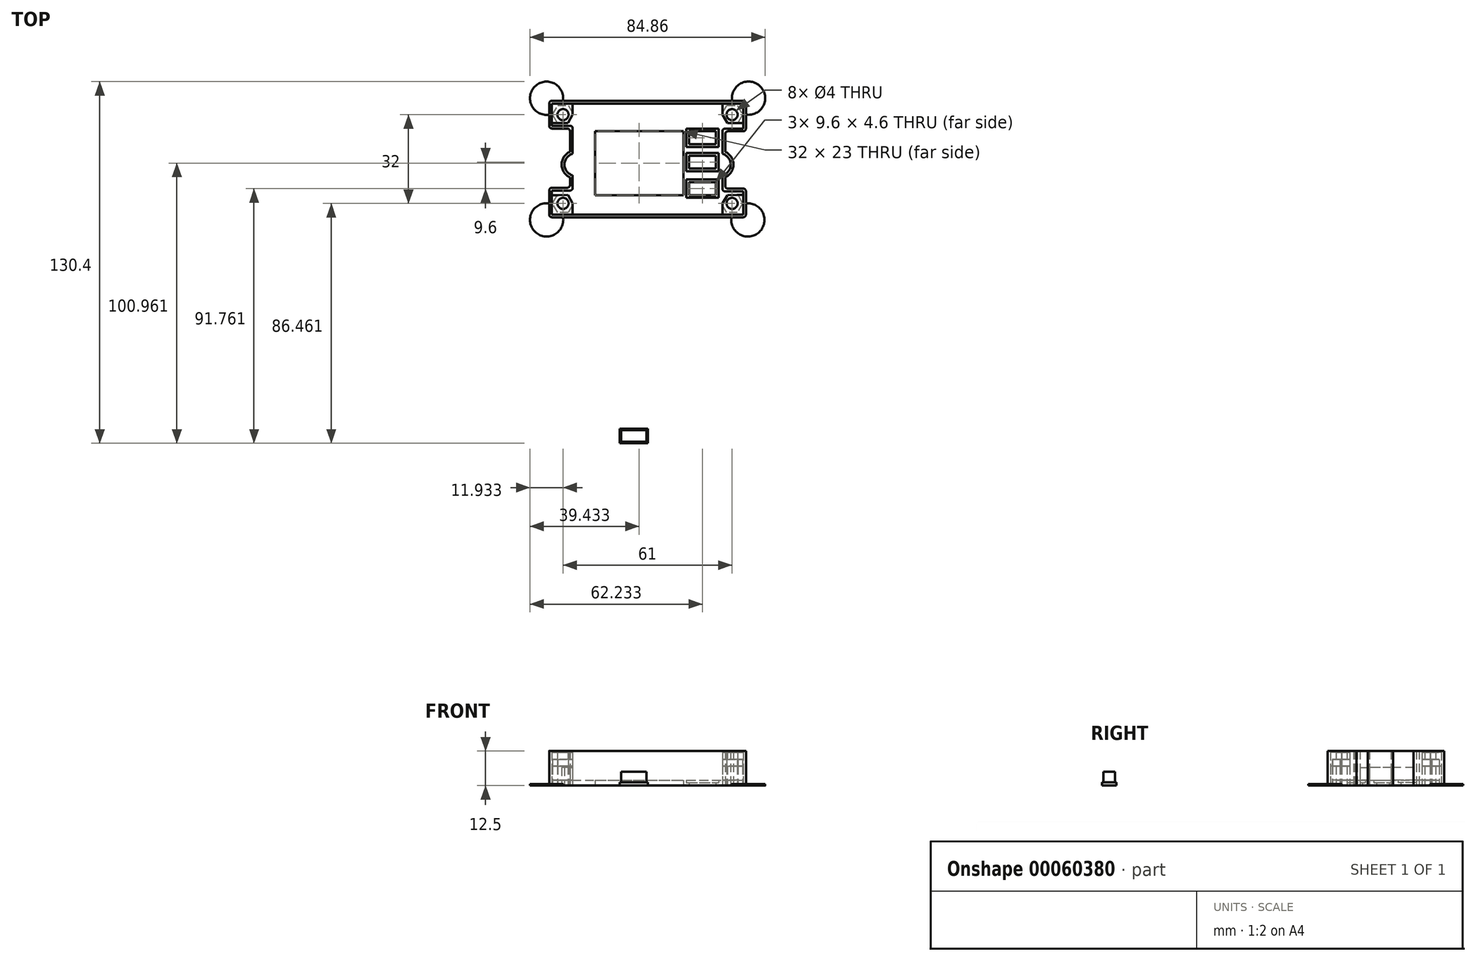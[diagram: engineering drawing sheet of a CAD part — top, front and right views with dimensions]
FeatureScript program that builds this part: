
annotation { "Feature Type Name" : "Feature", "Feature Type Description" : "" }
export const myFeature = defineFeature(function(context is Context, id is Id, definition is map)
    precondition{}
    {
        {
            var Q0;
            Q0=qCreatedBy(makeId("Top.planeOp"),FACE);
            var sketch = newSketch(context, id + "F0", { "sketchPlane" : qUnion([Q0])});
            skCircle(sketch, "E0.cCircle", {"center": v(0, 0) * mm, "radius": 3 * mm, "construction": true});
            skLineSegment(sketch, "E0.0", {"start": v(1.73, 3) * mm, "end": v(3.46, 0) * mm});
            skLineSegment(sketch, "E0.1", {"start": v(3.46, 0) * mm, "end": v(1.74, -3) * mm});
            skLineSegment(sketch, "E0.2", {"start": v(1.74, -3) * mm, "end": v(-1.73, -3) * mm});
            skLineSegment(sketch, "E0.3", {"start": v(-1.73, -3) * mm, "end": v(-3.46, 0) * mm});
            skLineSegment(sketch, "E0.4", {"start": v(-3.46, 0) * mm, "end": v(-1.74, 3) * mm});
            skLineSegment(sketch, "E0.5", {"start": v(-1.74, 3) * mm, "end": v(1.73, 3) * mm});
            skPoint(sketch, "E0.0.midPoint", {"position": v(2.6, 1.5) * mm});
            skCircle(sketch, "E1", {"center": v(0, 0) * mm, "radius": 1.5 * mm});
            skLineSegment(sketch, "E2.bottom", {"start": v(-12.76, 69.41) * mm, "end": v(56.24, 69.41) * mm});
            skLineSegment(sketch, "E2.top", {"start": v(-12.76, 29.41) * mm, "end": v(56.24, 29.41) * mm});
            skLineSegment(sketch, "E2.left", {"start": v(-12.76, 69.41) * mm, "end": v(-12.76, 29.41) * mm});
            skLineSegment(sketch, "E2.right", {"start": v(56.24, 69.41) * mm, "end": v(56.24, 29.41) * mm});
            skPoint(sketch, "E3.0.midPoint", {"position": v(-6.16, 66.92) * mm});
            skLineSegment(sketch, "E3.3", {"start": v(-10.48, 62.4) * mm, "end": v(-12.22, 65.4) * mm, "construction": true});
            skLineSegment(sketch, "E3.2", {"start": v(-7.02, 62.41) * mm, "end": v(-10.48, 62.4) * mm});
            skLineSegment(sketch, "E3.1", {"start": v(-5.3, 65.42) * mm, "end": v(-7.02, 62.41) * mm});
            skLineSegment(sketch, "E3.0", {"start": v(-7.03, 68.41) * mm, "end": v(-5.3, 65.42) * mm, "construction": true});
            skLineSegment(sketch, "E3.4", {"start": v(-12.22, 65.4) * mm, "end": v(-10.5, 68.4) * mm, "construction": true});
            skLineSegment(sketch, "E3.5", {"start": v(-10.5, 68.4) * mm, "end": v(-7.03, 68.41) * mm, "construction": true});
            skCircle(sketch, "E4", {"center": v(-8.76, 65.41) * mm, "radius": 1.5 * mm, "construction": true});
            skCircle(sketch, "E3.cCircle", {"center": v(-8.76, 65.41) * mm, "radius": 3 * mm, "construction": true});
            skPoint(sketch, "E5.0.midPoint", {"position": v(-6.16, 34.92) * mm});
            skLineSegment(sketch, "E5.3", {"start": v(-10.48, 30.4) * mm, "end": v(-12.22, 33.4) * mm, "construction": true});
            skLineSegment(sketch, "E5.2", {"start": v(-7.02, 30.41) * mm, "end": v(-10.48, 30.4) * mm, "construction": true});
            skLineSegment(sketch, "E5.1", {"start": v(-5.3, 33.42) * mm, "end": v(-7.02, 30.41) * mm, "construction": true});
            skLineSegment(sketch, "E5.0", {"start": v(-7.03, 36.41) * mm, "end": v(-5.3, 33.42) * mm});
            skLineSegment(sketch, "E5.4", {"start": v(-12.22, 33.4) * mm, "end": v(-10.5, 36.4) * mm, "construction": true});
            skLineSegment(sketch, "E5.5", {"start": v(-10.5, 36.4) * mm, "end": v(-7.03, 36.41) * mm});
            skCircle(sketch, "E6", {"center": v(-8.76, 33.41) * mm, "radius": 1.5 * mm, "construction": true});
            skCircle(sketch, "E5.cCircle", {"center": v(-8.76, 33.41) * mm, "radius": 3 * mm, "construction": true});
            skPoint(sketch, "E7.0.midPoint", {"position": v(54.84, 66.92) * mm});
            skLineSegment(sketch, "E7.3", {"start": v(50.52, 62.4) * mm, "end": v(48.78, 65.4) * mm});
            skLineSegment(sketch, "E7.2", {"start": v(53.98, 62.41) * mm, "end": v(50.52, 62.4) * mm});
            skLineSegment(sketch, "E7.1", {"start": v(55.7, 65.42) * mm, "end": v(53.98, 62.41) * mm, "construction": true});
            skLineSegment(sketch, "E7.0", {"start": v(53.97, 68.41) * mm, "end": v(55.7, 65.42) * mm, "construction": true});
            skLineSegment(sketch, "E7.4", {"start": v(48.78, 65.4) * mm, "end": v(50.5, 68.4) * mm, "construction": true});
            skLineSegment(sketch, "E7.5", {"start": v(50.5, 68.4) * mm, "end": v(53.97, 68.41) * mm, "construction": true});
            skCircle(sketch, "E8", {"center": v(52.24, 65.41) * mm, "radius": 1.5 * mm, "construction": true});
            skCircle(sketch, "E7.cCircle", {"center": v(52.24, 65.41) * mm, "radius": 3 * mm, "construction": true});
            skPoint(sketch, "E9.0.midPoint", {"position": v(54.84, 34.92) * mm});
            skLineSegment(sketch, "E9.3", {"start": v(50.52, 30.4) * mm, "end": v(48.78, 33.4) * mm, "construction": true});
            skLineSegment(sketch, "E9.2", {"start": v(53.98, 30.41) * mm, "end": v(50.52, 30.4) * mm, "construction": true});
            skLineSegment(sketch, "E9.1", {"start": v(55.7, 33.42) * mm, "end": v(53.98, 30.41) * mm, "construction": true});
            skLineSegment(sketch, "E9.0", {"start": v(53.97, 36.41) * mm, "end": v(55.7, 33.42) * mm, "construction": true});
            skLineSegment(sketch, "E9.4", {"start": v(48.78, 33.4) * mm, "end": v(50.5, 36.4) * mm});
            skLineSegment(sketch, "E9.5", {"start": v(50.5, 36.4) * mm, "end": v(53.97, 36.41) * mm});
            skCircle(sketch, "E10", {"center": v(52.24, 33.41) * mm, "radius": 1.5 * mm, "construction": true});
            skCircle(sketch, "E9.cCircle", {"center": v(52.24, 33.41) * mm, "radius": 3 * mm, "construction": true});
            skLineSegment(sketch, "E11", {"start": v(48.78, 33.4) * mm, "end": v(48.78, 29.41) * mm});
            skLineSegment(sketch, "E12", {"start": v(53.97, 36.41) * mm, "end": v(56.24, 36.41) * mm});
            skCircle(sketch, "E13.0", {"center": v(52.24, 33.41) * mm, "radius": 2 * mm});
            skLineSegment(sketch, "E14.0", {"start": v(50.34, 30.1) * mm, "end": v(48.52, 33.25) * mm});
            skLineSegment(sketch, "E14.1", {"start": v(54.15, 30.11) * mm, "end": v(50.34, 30.1) * mm});
            skLineSegment(sketch, "E14.2", {"start": v(56.05, 33.42) * mm, "end": v(54.15, 30.11) * mm});
            skLineSegment(sketch, "E14.3", {"start": v(54.23, 36.56) * mm, "end": v(56.05, 33.42) * mm});
            skLineSegment(sketch, "E15", {"start": v(-5.3, 33.42) * mm, "end": v(-5.3, 29.41) * mm});
            skLineSegment(sketch, "E16", {"start": v(-10.5, 36.4) * mm, "end": v(-12.76, 36.4) * mm});
            skLineSegment(sketch, "E17", {"start": v(-10.48, 62.4) * mm, "end": v(-12.76, 62.4) * mm});
            skLineSegment(sketch, "E18", {"start": v(-5.3, 65.42) * mm, "end": v(-5.3, 69.41) * mm});
            skLineSegment(sketch, "E19", {"start": v(53.98, 62.41) * mm, "end": v(56.24, 62.42) * mm});
            skLineSegment(sketch, "E20", {"start": v(48.78, 65.4) * mm, "end": v(48.78, 69.41) * mm});
            skCircle(sketch, "E21.0", {"center": v(52.24, 65.41) * mm, "radius": 2 * mm});
            skCircle(sketch, "E22.0", {"center": v(-8.76, 65.41) * mm, "radius": 2 * mm});
            skCircle(sketch, "E23.0", {"center": v(-8.76, 33.41) * mm, "radius": 2 * mm});
            skLineSegment(sketch, "E24.0", {"start": v(-6.86, 68.71) * mm, "end": v(-5.03, 65.57) * mm});
            skLineSegment(sketch, "E24.1", {"start": v(-10.67, 68.7) * mm, "end": v(-6.86, 68.71) * mm});
            skLineSegment(sketch, "E24.2", {"start": v(-12.57, 65.4) * mm, "end": v(-10.67, 68.7) * mm});
            skLineSegment(sketch, "E24.3", {"start": v(-10.74, 62.26) * mm, "end": v(-12.57, 65.4) * mm});
            skLineSegment(sketch, "E25.0", {"start": v(-12.57, 33.4) * mm, "end": v(-10.76, 36.56) * mm});
            skLineSegment(sketch, "E25.1", {"start": v(-10.66, 30.1) * mm, "end": v(-12.57, 33.4) * mm});
            skLineSegment(sketch, "E25.2", {"start": v(-6.85, 30.11) * mm, "end": v(-10.66, 30.1) * mm});
            skLineSegment(sketch, "E25.3", {"start": v(-5.03, 33.27) * mm, "end": v(-6.85, 30.11) * mm});
            skLineSegment(sketch, "E26.0", {"start": v(56.05, 65.42) * mm, "end": v(49.92, 54.75) * mm});
            skLineSegment(sketch, "E26.1", {"start": v(54.14, 68.71) * mm, "end": v(56.05, 65.42) * mm});
            skLineSegment(sketch, "E26.2", {"start": v(50.33, 68.7) * mm, "end": v(54.14, 68.71) * mm});
            skLineSegment(sketch, "E26.3", {"start": v(48.52, 65.55) * mm, "end": v(50.33, 68.7) * mm});
            skPoint(sketch, "E27", {"position": v(2.74, 36.41) * mm});
            skLineSegment(sketch, "E28.bottom", {"start": v(2.74, 36.41) * mm, "end": v(34.74, 36.41) * mm});
            skLineSegment(sketch, "E28.top", {"start": v(2.74, 59.41) * mm, "end": v(34.74, 59.41) * mm});
            skLineSegment(sketch, "E28.left", {"start": v(2.74, 36.41) * mm, "end": v(2.74, 59.41) * mm});
            skLineSegment(sketch, "E28.right", {"start": v(34.74, 36.41) * mm, "end": v(34.74, 59.41) * mm});
            skPoint(sketch, "E29", {"position": v(36.74, 59.41) * mm});
            skLineSegment(sketch, "E30.bottom", {"start": v(36.74, 59.41) * mm, "end": v(46.34, 59.41) * mm});
            skLineSegment(sketch, "E30.top", {"start": v(36.74, 54.81) * mm, "end": v(46.34, 54.81) * mm});
            skLineSegment(sketch, "E30.left", {"start": v(36.74, 59.41) * mm, "end": v(36.74, 54.81) * mm});
            skLineSegment(sketch, "E30.right", {"start": v(46.34, 59.41) * mm, "end": v(46.34, 54.81) * mm});
            skLineSegment(sketch, "E31.bottom", {"start": v(36.74, 36.41) * mm, "end": v(46.34, 36.41) * mm});
            skLineSegment(sketch, "E31.top", {"start": v(36.74, 41.01) * mm, "end": v(46.34, 41.01) * mm});
            skLineSegment(sketch, "E31.left", {"start": v(36.74, 36.41) * mm, "end": v(36.74, 41.01) * mm});
            skLineSegment(sketch, "E31.right", {"start": v(46.34, 36.41) * mm, "end": v(46.34, 41.01) * mm});
            skLineSegment(sketch, "E32.bottom", {"start": v(36.74, 46.01) * mm, "end": v(46.34, 46.01) * mm});
            skLineSegment(sketch, "E32.top", {"start": v(36.74, 50.61) * mm, "end": v(46.34, 50.61) * mm});
            skLineSegment(sketch, "E32.left", {"start": v(36.74, 46.01) * mm, "end": v(36.74, 50.61) * mm});
            skLineSegment(sketch, "E32.right", {"start": v(46.34, 46.01) * mm, "end": v(46.34, 50.61) * mm});
            skLineSegment(sketch, "E33.0", {"start": v(-13.76, 38.03) * mm, "end": v(-13.76, 29.41) * mm});
            skLineSegment(sketch, "E33.1", {"start": v(-12.76, 70.41) * mm, "end": v(56.24, 70.41) * mm});
            skLineSegment(sketch, "E33.2", {"start": v(57.24, 69.41) * mm, "end": v(57.24, 60.41) * mm});
            skLineSegment(sketch, "E33.3", {"start": v(-12.76, 28.41) * mm, "end": v(56.24, 28.41) * mm});
            skPoint(sketch, "E34", {"position": v(-13.76, 61.41) * mm});
            skPoint(sketch, "E35", {"position": v(-13.76, 40.41) * mm});
            skLineSegment(sketch, "E36", {"start": v(-13.76, 61.41) * mm, "end": v(-12.76, 61.41) * mm});
            skLineSegment(sketch, "E37", {"start": v(-13.76, 40.41) * mm, "end": v(-12.76, 40.41) * mm});
            skLineSegment(sketch, "E38.bottom", {"start": v(13.09, -34.33) * mm, "end": v(22.29, -34.33) * mm});
            skLineSegment(sketch, "E38.top", {"start": v(13.09, -38.53) * mm, "end": v(22.29, -38.53) * mm});
            skLineSegment(sketch, "E38.left", {"start": v(13.09, -34.33) * mm, "end": v(13.09, -38.53) * mm});
            skLineSegment(sketch, "E38.right", {"start": v(22.29, -34.33) * mm, "end": v(22.29, -38.53) * mm});
            skLineSegment(sketch, "E39.0", {"start": v(12.09, -33.33) * mm, "end": v(23.29, -33.33) * mm});
            skLineSegment(sketch, "E39.1", {"start": v(12.09, -33.33) * mm, "end": v(12.09, -39.53) * mm});
            skLineSegment(sketch, "E39.2", {"start": v(12.09, -39.53) * mm, "end": v(23.29, -39.53) * mm});
            skLineSegment(sketch, "E39.3", {"start": v(23.29, -33.33) * mm, "end": v(23.29, -39.53) * mm});
            skLineSegment(sketch, "E40.bottom", {"start": v(12.2, -48.35) * mm, "end": v(21.4, -48.35) * mm});
            skLineSegment(sketch, "E40.top", {"start": v(12.2, -52.55) * mm, "end": v(21.4, -52.55) * mm});
            skLineSegment(sketch, "E40.left", {"start": v(12.2, -48.35) * mm, "end": v(12.2, -52.55) * mm});
            skLineSegment(sketch, "E40.right", {"start": v(21.4, -48.35) * mm, "end": v(21.4, -52.55) * mm});
            skLineSegment(sketch, "E41.0", {"start": v(11.7, -47.85) * mm, "end": v(21.9, -47.85) * mm});
            skLineSegment(sketch, "E41.1", {"start": v(11.7, -47.85) * mm, "end": v(11.7, -53.05) * mm});
            skLineSegment(sketch, "E41.2", {"start": v(11.7, -53.05) * mm, "end": v(21.9, -53.05) * mm});
            skLineSegment(sketch, "E41.3", {"start": v(21.9, -47.85) * mm, "end": v(21.9, -53.05) * mm});
            skArc(sketch, "E42", {"start": v(57.24, 65.42) * mm, "mid": v(62.4, 75.6) * mm, "end": v(52.24, 70.41) * mm});
            skArc(sketch, "E43", {"start": v(52.24, 29.41) * mm, "mid": v(61.67, 22.77) * mm, "end": v(57.24, 33.42) * mm});
            skArc(sketch, "E44", {"start": v(-13.76, 33.4) * mm, "mid": v(-18.92, 23.23) * mm, "end": v(-8.76, 28.41) * mm});
            skArc(sketch, "E45", {"start": v(-8.76, 70.41) * mm, "mid": v(-18.93, 75.57) * mm, "end": v(-13.76, 65.4) * mm});
            skLineSegment(sketch, "E46.0", {"start": v(35.74, 53.81) * mm, "end": v(47.34, 53.81) * mm});
            skLineSegment(sketch, "E46.1", {"start": v(35.74, 60.41) * mm, "end": v(35.74, 53.81) * mm});
            skLineSegment(sketch, "E46.2", {"start": v(35.74, 60.41) * mm, "end": v(47.34, 60.41) * mm});
            skLineSegment(sketch, "E46.3", {"start": v(47.34, 60.41) * mm, "end": v(47.34, 53.81) * mm});
            skLineSegment(sketch, "E47.0", {"start": v(35.74, 51.61) * mm, "end": v(47.34, 51.61) * mm});
            skLineSegment(sketch, "E47.1", {"start": v(35.74, 45.01) * mm, "end": v(35.74, 51.61) * mm});
            skLineSegment(sketch, "E47.2", {"start": v(35.74, 45.01) * mm, "end": v(47.34, 45.01) * mm});
            skLineSegment(sketch, "E47.3", {"start": v(47.34, 45.01) * mm, "end": v(47.34, 51.61) * mm});
            skLineSegment(sketch, "E48.0", {"start": v(35.74, 42.01) * mm, "end": v(47.34, 42.01) * mm});
            skLineSegment(sketch, "E48.1", {"start": v(35.74, 35.41) * mm, "end": v(35.74, 42.01) * mm});
            skLineSegment(sketch, "E48.2", {"start": v(35.74, 35.41) * mm, "end": v(47.34, 35.41) * mm});
            skLineSegment(sketch, "E48.3", {"start": v(47.34, 35.41) * mm, "end": v(47.34, 42.01) * mm});
            skLineSegment(sketch, "E49", {"start": v(-4.26, 32.41) * mm, "end": v(47.74, 32.41) * mm, "construction": true});
            skLineSegment(sketch, "E50", {"start": v(47.74, 32.41) * mm, "end": v(47.74, 68.41) * mm, "construction": true});
            skLineSegment(sketch, "E51", {"start": v(47.74, 68.41) * mm, "end": v(-4.26, 68.41) * mm, "construction": true});
            skLineSegment(sketch, "E52", {"start": v(-4.26, 68.41) * mm, "end": v(-4.26, 32.41) * mm, "construction": true});
            skArc(sketch, "E53", {"start": v(-4.26, 50.41) * mm, "mid": v(-7.26, 47.41) * mm, "end": v(-4.26, 44.41) * mm, "construction": true});
            skArc(sketch, "E54", {"start": v(47.74, 44.41) * mm, "mid": v(50.74, 47.41) * mm, "end": v(47.74, 50.41) * mm, "construction": true});
            skArc(sketch, "E55.0", {"start": v(-4.26, 51.41) * mm, "mid": v(-4.76, 51.38) * mm, "end": v(-5.26, 51.28) * mm});
            skArc(sketch, "E56.0", {"start": v(47.74, 43.41) * mm, "mid": v(48.33, 43.45) * mm, "end": v(48.9, 43.58) * mm});
            skLineSegment(sketch, "E57", {"start": v(-12.76, 61.41) * mm, "end": v(-6.26, 61.41) * mm});
            skLineSegment(sketch, "E58", {"start": v(-5.26, 60.41) * mm, "end": v(-5.26, 51.28) * mm});
            skLineSegment(sketch, "E59", {"start": v(-12.76, 38.03) * mm, "end": v(-6.26, 38.03) * mm});
            skLineSegment(sketch, "E60", {"start": v(-5.26, 39.03) * mm, "end": v(-5.26, 43.54) * mm});
            skArc(sketch, "E61", {"start": v(-5.26, 51.28) * mm, "mid": v(-8.26, 47.41) * mm, "end": v(-5.26, 43.54) * mm});
            skArc(sketch, "E62", {"start": v(-5.26, 43.54) * mm, "mid": v(-4.76, 43.44) * mm, "end": v(-4.26, 43.41) * mm});
            skLineSegment(sketch, "E63.0", {"start": v(-12.76, 39.03) * mm, "end": v(-7.26, 39.03) * mm});
            skLineSegment(sketch, "E63.1", {"start": v(-12.76, 60.41) * mm, "end": v(-7.26, 60.41) * mm});
            skLineSegment(sketch, "E63.2", {"start": v(-6.26, 59.41) * mm, "end": v(-6.26, 52) * mm});
            skArc(sketch, "E63.3", {"start": v(-6.26, 52) * mm, "mid": v(-9.26, 47.41) * mm, "end": v(-6.26, 42.83) * mm});
            skLineSegment(sketch, "E63.4", {"start": v(-6.26, 40.03) * mm, "end": v(-6.26, 42.83) * mm});
            skLineSegment(sketch, "E64", {"start": v(-12.76, 60.41) * mm, "end": v(-12.76, 60.41) * mm});
            skLineSegment(sketch, "E65", {"start": v(-12.76, 39.03) * mm, "end": v(-12.76, 39.03) * mm});
            skArc(sketch, "E66.filletArc", {"start": v(-12.76, 39.03) * mm, "mid": v(-13.46, 38.74) * mm, "end": v(-13.76, 38.03) * mm});
            skLineSegment(sketch, "E67", {"start": v(-13.76, 69.41) * mm, "end": v(-13.76, 61.41) * mm});
            skPoint(sketch, "E68.visualSharp", {"position": v(-13.76, 60.41) * mm});
            skArc(sketch, "E68.filletArc", {"start": v(-13.76, 61.41) * mm, "mid": v(-13.46, 60.7) * mm, "end": v(-12.76, 60.41) * mm});
            skPoint(sketch, "E69.visualSharp", {"position": v(-5.26, 61.41) * mm});
            skArc(sketch, "E69.filletArc", {"start": v(-5.26, 60.41) * mm, "mid": v(-5.55, 61.12) * mm, "end": v(-6.26, 61.41) * mm});
            skArc(sketch, "E70.filletArc", {"start": v(-6.26, 59.41) * mm, "mid": v(-6.55, 60.12) * mm, "end": v(-7.26, 60.41) * mm});
            skPoint(sketch, "E71.visualSharp", {"position": v(-6.26, 39.03) * mm});
            skArc(sketch, "E71.filletArc", {"start": v(-7.26, 39.03) * mm, "mid": v(-6.55, 39.32) * mm, "end": v(-6.26, 40.03) * mm});
            skPoint(sketch, "E72.visualSharp", {"position": v(-5.26, 38.03) * mm});
            skArc(sketch, "E72.filletArc", {"start": v(-6.26, 38.03) * mm, "mid": v(-5.55, 38.32) * mm, "end": v(-5.26, 39.03) * mm});
            skLineSegment(sketch, "E73", {"start": v(-6.26, 59.41) * mm, "end": v(-5.26, 59.41) * mm});
            skLineSegment(sketch, "E74", {"start": v(-6.26, 40.03) * mm, "end": v(-5.26, 40.03) * mm});
            skLineSegment(sketch, "E75", {"start": v(56.24, 60.41) * mm, "end": v(49.74, 60.41) * mm});
            skLineSegment(sketch, "E76", {"start": v(48.74, 59.41) * mm, "end": v(48.74, 51.28) * mm});
            skLineSegment(sketch, "E77", {"start": v(48.74, 43.54) * mm, "end": v(48.74, 38.74) * mm});
            skLineSegment(sketch, "E78", {"start": v(49.74, 37.74) * mm, "end": v(56.24, 37.74) * mm});
            skArc(sketch, "E79", {"start": v(48.74, 51.28) * mm, "mid": v(48.25, 51.38) * mm, "end": v(47.74, 51.41) * mm});
            skArc(sketch, "E80", {"start": v(48.9, 43.58) * mm, "mid": v(51.74, 47.5) * mm, "end": v(48.74, 51.28) * mm});
            skLineSegment(sketch, "E81.0", {"start": v(56.24, 59.41) * mm, "end": v(50.74, 59.41) * mm});
            skLineSegment(sketch, "E81.1", {"start": v(49.74, 58.41) * mm, "end": v(49.74, 52) * mm});
            skLineSegment(sketch, "E82.0", {"start": v(50.74, 38.74) * mm, "end": v(56.24, 38.74) * mm});
            skLineSegment(sketch, "E83", {"start": v(49.74, 42.83) * mm, "end": v(49.74, 39.74) * mm});
            skArc(sketch, "E84", {"start": v(49.74, 42.83) * mm, "mid": v(52.74, 47.41) * mm, "end": v(49.74, 52) * mm});
            skPoint(sketch, "E85.visualSharp", {"position": v(49.74, 59.41) * mm});
            skArc(sketch, "E85.filletArc", {"start": v(50.74, 59.41) * mm, "mid": v(50.04, 59.12) * mm, "end": v(49.74, 58.41) * mm});
            skPoint(sketch, "E86.visualSharp", {"position": v(49.74, 38.74) * mm});
            skArc(sketch, "E86.filletArc", {"start": v(49.74, 39.74) * mm, "mid": v(50.04, 39.04) * mm, "end": v(50.74, 38.74) * mm});
            skLineSegment(sketch, "E87", {"start": v(56.24, 38.74) * mm, "end": v(56.24, 38.74) * mm});
            skLineSegment(sketch, "E88", {"start": v(56.24, 59.41) * mm, "end": v(56.24, 59.41) * mm});
            skArc(sketch, "E89.filletArc", {"start": v(56.24, 59.41) * mm, "mid": v(56.95, 59.7) * mm, "end": v(57.24, 60.41) * mm});
            skLineSegment(sketch, "E90", {"start": v(57.24, 29.41) * mm, "end": v(57.24, 37.74) * mm});
            skPoint(sketch, "E91.visualSharp", {"position": v(57.24, 38.74) * mm});
            skArc(sketch, "E91.filletArc", {"start": v(57.24, 37.74) * mm, "mid": v(56.95, 38.45) * mm, "end": v(56.24, 38.74) * mm});
            skPoint(sketch, "E92.visualSharp", {"position": v(48.74, 37.74) * mm});
            skArc(sketch, "E92.filletArc", {"start": v(48.74, 38.74) * mm, "mid": v(49.04, 38.04) * mm, "end": v(49.74, 37.74) * mm});
            skPoint(sketch, "E93.visualSharp", {"position": v(48.74, 60.41) * mm});
            skArc(sketch, "E93.filletArc", {"start": v(49.74, 60.41) * mm, "mid": v(49.04, 60.12) * mm, "end": v(48.74, 59.41) * mm});
            skPoint(sketch, "E94.visualSharp", {"position": v(57.24, 28.41) * mm});
            skArc(sketch, "E94.filletArc", {"start": v(56.24, 28.41) * mm, "mid": v(56.95, 28.7) * mm, "end": v(57.24, 29.41) * mm});
            skPoint(sketch, "E95.visualSharp", {"position": v(-13.76, 28.41) * mm});
            skArc(sketch, "E95.filletArc", {"start": v(-13.76, 29.41) * mm, "mid": v(-13.46, 28.7) * mm, "end": v(-12.76, 28.41) * mm});
            skPoint(sketch, "E96.visualSharp", {"position": v(57.24, 70.41) * mm});
            skArc(sketch, "E96.filletArc", {"start": v(57.24, 69.41) * mm, "mid": v(56.95, 70.12) * mm, "end": v(56.24, 70.41) * mm});
            skPoint(sketch, "E97.visualSharp", {"position": v(-13.76, 70.41) * mm});
            skArc(sketch, "E97.filletArc", {"start": v(-12.76, 70.41) * mm, "mid": v(-13.46, 70.12) * mm, "end": v(-13.76, 69.41) * mm});
            skSolve(sketch);
        }
        {
            var Q0;
            {var subQ12=sQuery(id+"F0.wireOp",EDGE,"E14.1");Q0=makeQuery(id+"F0.imprint","IMPRINT",FACE,{"disambiguationData":[TD([[makeQuery(id+"F0.imprint","IMPRINT",EDGE,{"derivedFrom":subQ12}),1.0]])]});}
            var Q1;
            {var subQ6=sQuery(id+"F0.wireOp",EDGE,"E9.4");Q1=makeQuery(id+"F0.imprint","IMPRINT",FACE,{"disambiguationData":[TD([[makeQuery(id+"F0.imprint","IMPRINT",EDGE,{"derivedFrom":subQ6}),-1.0]])]});}
            var Q2;
            {var subQ5=sQuery(id+"F0.wireOp",EDGE,"E25.1");Q2=makeQuery(id+"F0.imprint","IMPRINT",FACE,{"disambiguationData":[TD([[makeQuery(id+"F0.imprint","IMPRINT",EDGE,{"derivedFrom":subQ5}),1.0]])]});}
            var Q3;
            {var subQ5=sQuery(id+"F0.wireOp",EDGE,"E5.0");Q3=makeQuery(id+"F0.imprint","IMPRINT",FACE,{"disambiguationData":[TD([[makeQuery(id+"F0.imprint","IMPRINT",EDGE,{"derivedFrom":subQ5}),-1.0]])]});}
            var Q4;
            {var subQ11=sQuery(id+"F0.wireOp",EDGE,"E24.1");Q4=makeQuery(id+"F0.imprint","IMPRINT",FACE,{"disambiguationData":[TD([[makeQuery(id+"F0.imprint","IMPRINT",EDGE,{"derivedFrom":subQ11}),1.0]])]});}
            var Q5;
            {var subQ5=sQuery(id+"F0.wireOp",EDGE,"E3.2");Q5=makeQuery(id+"F0.imprint","IMPRINT",FACE,{"disambiguationData":[TD([[makeQuery(id+"F0.imprint","IMPRINT",EDGE,{"derivedFrom":subQ5}),-1.0]])]});}
            var Q6;
            {var subQ7=sQuery(id+"F0.wireOp",EDGE,"E26.1");Q6=makeQuery(id+"F0.imprint","IMPRINT",FACE,{"disambiguationData":[TD([[makeQuery(id+"F0.imprint","IMPRINT",EDGE,{"derivedFrom":subQ7}),1.0]])]});}
            var Q7;
            {var subQ1=sQuery(id+"F0.wireOp",EDGE,"E7.3");Q7=makeQuery(id+"F0.imprint","IMPRINT",FACE,{"disambiguationData":[TD([[makeQuery(id+"F0.imprint","IMPRINT",EDGE,{"derivedFrom":subQ1}),-1.0]])]});}
            extrude(context, id + "F1", {"entities" : qUnion([Q0, Q1, Q2, Q3, Q4, Q5, Q6, Q7]), "depth" : 7 * mm});
        }
        {
            var Q0;
            {var subQ12=sQuery(id+"F0.wireOp",EDGE,"E14.1");Q0=makeQuery(id+"F0.imprint","IMPRINT",FACE,{"disambiguationData":[TD([[makeQuery(id+"F0.imprint","IMPRINT",EDGE,{"derivedFrom":subQ12}),1.0]])]});}
            var Q1;
            {var subQ7=sQuery(id+"F0.wireOp",EDGE,"E26.1");Q1=makeQuery(id+"F0.imprint","IMPRINT",FACE,{"disambiguationData":[TD([[makeQuery(id+"F0.imprint","IMPRINT",EDGE,{"derivedFrom":subQ7}),1.0]])]});}
            var Q2;
            {var subQ11=sQuery(id+"F0.wireOp",EDGE,"E24.1");Q2=makeQuery(id+"F0.imprint","IMPRINT",FACE,{"disambiguationData":[TD([[makeQuery(id+"F0.imprint","IMPRINT",EDGE,{"derivedFrom":subQ11}),1.0]])]});}
            var Q3;
            {var subQ5=sQuery(id+"F0.wireOp",EDGE,"E25.1");Q3=makeQuery(id+"F0.imprint","IMPRINT",FACE,{"disambiguationData":[TD([[makeQuery(id+"F0.imprint","IMPRINT",EDGE,{"derivedFrom":subQ5}),1.0]])]});}
            extrude(context, id + "F2", {"entities" : qUnion([Q0, Q1, Q2, Q3]), "endBound" : BoundingType.UP_TO_NEXT, "depth" : 25 * mm});
        }
        {
            var Q0;
            Q0=makeQuery(id+"F2.opExtrude","CAP_FACE",FACE,{"disambiguationData":[OSD([sQuery(id+"F0.wireOp",EDGE,"E2.top"),sQuery(id+"F0.wireOp",EDGE,"E2.right"),sQuery(id+"F0.wireOp",EDGE,"E9.4"),sQuery(id+"F0.wireOp",EDGE,"E9.5"),sQuery(id+"F0.wireOp",EDGE,"E11"),sQuery(id+"F0.wireOp",EDGE,"E12"),sQuery(id+"F0.wireOp",EDGE,"E13.0")])],"isStart":false});
            var Q1;
            Q1=makeQuery(id+"F2.opExtrude","CAP_FACE",FACE,{"disambiguationData":[OSD([sQuery(id+"F0.wireOp",EDGE,"E2.top"),sQuery(id+"F0.wireOp",EDGE,"E2.left"),sQuery(id+"F0.wireOp",EDGE,"E5.0"),sQuery(id+"F0.wireOp",EDGE,"E5.5"),sQuery(id+"F0.wireOp",EDGE,"E15"),sQuery(id+"F0.wireOp",EDGE,"E16"),sQuery(id+"F0.wireOp",EDGE,"E23.0")])],"isStart":false});
            var Q2;
            Q2=makeQuery(id+"F2.opExtrude","CAP_FACE",FACE,{"disambiguationData":[OSD([sQuery(id+"F0.wireOp",EDGE,"E2.bottom"),sQuery(id+"F0.wireOp",EDGE,"E2.left"),sQuery(id+"F0.wireOp",EDGE,"E3.2"),sQuery(id+"F0.wireOp",EDGE,"E3.1"),sQuery(id+"F0.wireOp",EDGE,"E17"),sQuery(id+"F0.wireOp",EDGE,"E18"),sQuery(id+"F0.wireOp",EDGE,"E22.0")])],"isStart":false});
            var Q3;
            Q3=makeQuery(id+"F2.opExtrude","CAP_FACE",FACE,{"disambiguationData":[OSD([sQuery(id+"F0.wireOp",EDGE,"E2.bottom"),sQuery(id+"F0.wireOp",EDGE,"E2.right"),sQuery(id+"F0.wireOp",EDGE,"E7.3"),sQuery(id+"F0.wireOp",EDGE,"E7.2"),sQuery(id+"F0.wireOp",EDGE,"E19"),sQuery(id+"F0.wireOp",EDGE,"E20"),sQuery(id+"F0.wireOp",EDGE,"E21.0")])],"isStart":false});
            extrude(context, id + "F3", {"entities" : qUnion([Q0, Q1, Q2, Q3]), "depth" : 2.5 * mm});
        }
        {
            var Q0;
            Q0=makeQuery(id+"F1.opExtrude","CAP_FACE",FACE,{"disambiguationData":[OSD([sQuery(id+"F0.wireOp",EDGE,"E2.top"),sQuery(id+"F0.wireOp",EDGE,"E2.right"),sQuery(id+"F0.wireOp",EDGE,"E9.4"),sQuery(id+"F0.wireOp",EDGE,"E9.5"),sQuery(id+"F0.wireOp",EDGE,"E11"),sQuery(id+"F0.wireOp",EDGE,"E12"),sQuery(id+"F0.wireOp",EDGE,"E13.0")])],"isStart":false});
            var Q1;
            Q1=makeQuery(id+"F1.opExtrude","CAP_FACE",FACE,{"disambiguationData":[OSD([sQuery(id+"F0.wireOp",EDGE,"E2.top"),sQuery(id+"F0.wireOp",EDGE,"E2.left"),sQuery(id+"F0.wireOp",EDGE,"E5.0"),sQuery(id+"F0.wireOp",EDGE,"E5.5"),sQuery(id+"F0.wireOp",EDGE,"E15"),sQuery(id+"F0.wireOp",EDGE,"E16"),sQuery(id+"F0.wireOp",EDGE,"E23.0")])],"isStart":false});
            var Q2;
            Q2=makeQuery(id+"F1.opExtrude","CAP_FACE",FACE,{"disambiguationData":[OSD([sQuery(id+"F0.wireOp",EDGE,"E2.bottom"),sQuery(id+"F0.wireOp",EDGE,"E2.left"),sQuery(id+"F0.wireOp",EDGE,"E3.2"),sQuery(id+"F0.wireOp",EDGE,"E3.1"),sQuery(id+"F0.wireOp",EDGE,"E17"),sQuery(id+"F0.wireOp",EDGE,"E18"),sQuery(id+"F0.wireOp",EDGE,"E22.0")])],"isStart":false});
            var Q3;
            Q3=makeQuery(id+"F1.opExtrude","CAP_FACE",FACE,{"disambiguationData":[OSD([sQuery(id+"F0.wireOp",EDGE,"E2.bottom"),sQuery(id+"F0.wireOp",EDGE,"E2.right"),sQuery(id+"F0.wireOp",EDGE,"E7.3"),sQuery(id+"F0.wireOp",EDGE,"E7.2"),sQuery(id+"F0.wireOp",EDGE,"E19"),sQuery(id+"F0.wireOp",EDGE,"E20"),sQuery(id+"F0.wireOp",EDGE,"E21.0")])],"isStart":false});
            extrude(context, id + "F4", {"entities" : qUnion([Q0, Q1, Q2, Q3]), "operationType" : NewBodyOperationType.ADD, "depth" : 5 * mm, "hasSecondDirection" : true, "secondDirectionOppositeDirection" : false, "secondDirectionDepth" : 2.5 * mm});
        }
        {
            var Q0;
            {var subQ14=sQuery(id+"F0.wireOp",EDGE,"E3.2");Q0=makeQuery(id+"F0.imprint","IMPRINT",FACE,{"disambiguationData":[TD([[makeQuery(id+"F0.imprint","IMPRINT",EDGE,{"derivedFrom":subQ14}),1.0]])]});}
            var Q1;
            Q1=makeQuery(id+"F0.imprint","IMPRINT",FACE,{"disambiguationData":[TD([[makeQuery(id+"F0.imprint","IMPRINT",EDGE,{"derivedFrom":sQuery(id+"F0.wireOp",EDGE,"E22.0")}),1.0]])]});
            var Q2;
            Q2=makeQuery(id+"F0.imprint","IMPRINT",FACE,{"disambiguationData":[TD([[makeQuery(id+"F0.imprint","IMPRINT",EDGE,{"derivedFrom":sQuery(id+"F0.wireOp",EDGE,"E21.0")}),1.0]])]});
            var Q3;
            Q3=makeQuery(id+"F0.imprint","IMPRINT",FACE,{"disambiguationData":[TD([[makeQuery(id+"F0.imprint","IMPRINT",EDGE,{"derivedFrom":sQuery(id+"F0.wireOp",EDGE,"E13.0")}),1.0]])]});
            var Q4;
            Q4=makeQuery(id+"F0.imprint","IMPRINT",FACE,{"disambiguationData":[TD([[makeQuery(id+"F0.imprint","IMPRINT",EDGE,{"derivedFrom":sQuery(id+"F0.wireOp",EDGE,"E23.0")}),1.0]])]});
            var Q5;
            {var subQ0=sQuery(id+"F0.wireOp",EDGE,"E19");var subQ1=sQuery(id+"F0.wireOp",EDGE,"E2.right");var subQ2=makeQuery(id+"F0.imprint","INTERSECT",VERTEX,{"derivedFrom":[subQ1,subQ0]});Q5=makeQuery(id+"F0.imprint","IMPRINT",FACE,{"disambiguationData":[TD([[makeQuery(id+"F0.imprint","IMPRINT",EDGE,{"disambiguationData":[TD([[subQ2,-1.0]])],"derivedFrom":subQ1}),-1.0]])]});}
            extrude(context, id + "F5", {"entities" : qUnion([Q0, Q1, Q2, Q3, Q4, Q5]), "depth" : 2 * mm});
        }
        {
            var Q0;
            Q0=makeQuery(id+"F0.imprint","IMPRINT",FACE,{"disambiguationData":[TD([[makeQuery(id+"F0.imprint","IMPRINT",EDGE,{"derivedFrom":sQuery(id+"F0.wireOp",EDGE,"E30.bottom")}),1.0]])]});
            var Q1;
            Q1=makeQuery(id+"F0.imprint","IMPRINT",FACE,{"disambiguationData":[TD([[makeQuery(id+"F0.imprint","IMPRINT",EDGE,{"derivedFrom":sQuery(id+"F0.wireOp",EDGE,"E32.bottom")}),-1.0]])]});
            var Q2;
            Q2=makeQuery(id+"F0.imprint","IMPRINT",FACE,{"disambiguationData":[TD([[makeQuery(id+"F0.imprint","IMPRINT",EDGE,{"derivedFrom":sQuery(id+"F0.wireOp",EDGE,"E31.bottom")}),-1.0]])]});
            extrude(context, id + "F6", {"entities" : qUnion([Q0, Q1, Q2]), "operationType" : NewBodyOperationType.ADD, "depth" : 1 * mm});
        }
        {
            var Q0;
            {var subQ18=sQuery(id+"F0.wireOp",EDGE,"E33.1");Q0=makeQuery(id+"F0.imprint","IMPRINT",FACE,{"disambiguationData":[TD([[makeQuery(id+"F0.imprint","IMPRINT",EDGE,{"derivedFrom":subQ18}),-1.0]])]});}
            var Q1;
            {var subQ0=sQuery(id+"F0.wireOp",EDGE,"E37");Q1=makeQuery(id+"F0.imprint","IMPRINT",FACE,{"disambiguationData":[TD([[makeQuery(id+"F0.imprint","IMPRINT",EDGE,{"derivedFrom":subQ0}),-1.0]])]});}
            var Q2;
            {var subQ8=sQuery(id+"F0.wireOp",EDGE,"E66.filletArc");Q2=makeQuery(id+"F0.imprint","IMPRINT",FACE,{"disambiguationData":[TD([[makeQuery(id+"F0.imprint","IMPRINT",EDGE,{"derivedFrom":subQ8}),1.0]])]});}
            var Q3;
            {var subQ1=sQuery(id+"F0.wireOp",EDGE,"E59");Q3=makeQuery(id+"F0.imprint","IMPRINT",FACE,{"disambiguationData":[TD([[makeQuery(id+"F0.imprint","IMPRINT",EDGE,{"derivedFrom":subQ1}),1.0]])]});}
            var Q4;
            {var subQ4=sQuery(id+"F0.wireOp",EDGE,"E57");Q4=makeQuery(id+"F0.imprint","IMPRINT",FACE,{"disambiguationData":[TD([[makeQuery(id+"F0.imprint","IMPRINT",EDGE,{"derivedFrom":subQ4}),-1.0]])]});}
            var Q5;
            {var subQ0=sQuery(id+"F0.wireOp",EDGE,"E36");Q5=makeQuery(id+"F0.imprint","IMPRINT",FACE,{"disambiguationData":[TD([[makeQuery(id+"F0.imprint","IMPRINT",EDGE,{"derivedFrom":subQ0}),-1.0]])]});}
            var Q6;
            Q6=makeQuery(id+"F0.imprint","IMPRINT",FACE,{"disambiguationData":[TD([[makeQuery(id+"F0.imprint","IMPRINT",EDGE,{"derivedFrom":sQuery(id+"F0.wireOp",EDGE,"E76")}),1.0]])]});
            var Q7;
            {var subQ3=sQuery(id+"F0.wireOp",EDGE,"E81.0");var subQ5=sQuery(id+"F0.wireOp",EDGE,"E26.0");var subQ7=makeQuery(id+"F0.imprint","INTERSECT",VERTEX,{"derivedFrom":[subQ5,subQ3]});Q7=makeQuery(id+"F0.imprint","IMPRINT",FACE,{"disambiguationData":[TD([[makeQuery(id+"F0.imprint","IMPRINT",EDGE,{"disambiguationData":[TD([[subQ7,1.0]])],"derivedFrom":subQ5}),1.0]])]});}
            var Q8;
            {var subQ2=sQuery(id+"F0.wireOp",EDGE,"E91.filletArc");Q8=makeQuery(id+"F0.imprint","IMPRINT",FACE,{"disambiguationData":[TD([[makeQuery(id+"F0.imprint","IMPRINT",EDGE,{"derivedFrom":subQ2}),1.0]])]});}
            extrude(context, id + "F7", {"entities" : qUnion([Q0, Q1, Q2, Q3, Q4, Q5, Q6, Q7, Q8]), "depth" : 12.5 * mm});
        }
        {
            var Q0;
            {var subQ0=sQuery(id+"F0.wireOp",EDGE,"E61");Q0=makeQuery(id+"F0.imprint","IMPRINT",FACE,{"disambiguationData":[TD([[makeQuery(id+"F0.imprint","IMPRINT",EDGE,{"derivedFrom":subQ0}),-1.0]])]});}
            extrude(context, id + "F8", {"entities" : qUnion([Q0]), "depth" : 6.5 * mm});
        }
        {
            var Q0;
            Q0=makeQuery(id+"F0.imprint","IMPRINT",FACE,{"disambiguationData":[TD([[makeQuery(id+"F0.imprint","IMPRINT",EDGE,{"derivedFrom":sQuery(id+"F0.wireOp",EDGE,"E40.bottom")}),1.0]])]});
            extrude(context, id + "F9", {"entities" : qUnion([Q0]), "depth" : 1.2 * mm});
        }
        {
            var Q0;
            Q0=makeQuery(id+"F0.imprint","IMPRINT",FACE,{"disambiguationData":[TD([[makeQuery(id+"F0.imprint","IMPRINT",EDGE,{"derivedFrom":sQuery(id+"F0.wireOp",EDGE,"E40.bottom")}),-1.0]])]});
            extrude(context, id + "F10", {"entities" : qUnion([Q0]), "operationType" : NewBodyOperationType.ADD, "depth" : 5 * mm});
        }
        {
            var Q0;
            {var subQ3=sQuery(id+"F0.wireOp",EDGE,"E44");Q0=makeQuery(id+"F0.imprint","IMPRINT",FACE,{"disambiguationData":[TD([[makeQuery(id+"F0.imprint","IMPRINT",EDGE,{"derivedFrom":subQ3}),1.0]])]});}
            var Q1;
            {var subQ3=sQuery(id+"F0.wireOp",EDGE,"E45");Q1=makeQuery(id+"F0.imprint","IMPRINT",FACE,{"disambiguationData":[TD([[makeQuery(id+"F0.imprint","IMPRINT",EDGE,{"derivedFrom":subQ3}),1.0]])]});}
            var Q2;
            {var subQ3=sQuery(id+"F0.wireOp",EDGE,"E42");Q2=makeQuery(id+"F0.imprint","IMPRINT",FACE,{"disambiguationData":[TD([[makeQuery(id+"F0.imprint","IMPRINT",EDGE,{"derivedFrom":subQ3}),1.0]])]});}
            var Q3;
            {var subQ0=sQuery(id+"F0.wireOp",EDGE,"E33.3");var subQ1=sQuery(id+"F0.wireOp",EDGE,"E33.2");var subQ2=makeQuery(id+"F0.imprint","INTERSECT",VERTEX,{"derivedFrom":[subQ1,subQ0]});Q3=makeQuery(id+"F0.imprint","IMPRINT",FACE,{"disambiguationData":[TD([[makeQuery(id+"F0.imprint","IMPRINT",EDGE,{"disambiguationData":[TD([[subQ2,1.0]])],"derivedFrom":subQ1}),1.0]])]});}
            var Q4;
            {var subQ0=sQuery(id+"F0.wireOp",EDGE,"E94.filletArc");Q4=makeQuery(id+"F0.imprint","IMPRINT",FACE,{"disambiguationData":[TD([[makeQuery(id+"F0.imprint","IMPRINT",EDGE,{"derivedFrom":subQ0}),-1.0]])]});}
            extrude(context, id + "F11", {"entities" : qUnion([Q0, Q1, Q2, Q3, Q4]), "operationType" : NewBodyOperationType.ADD, "depth" : 0.5 * mm});
        }
    });
